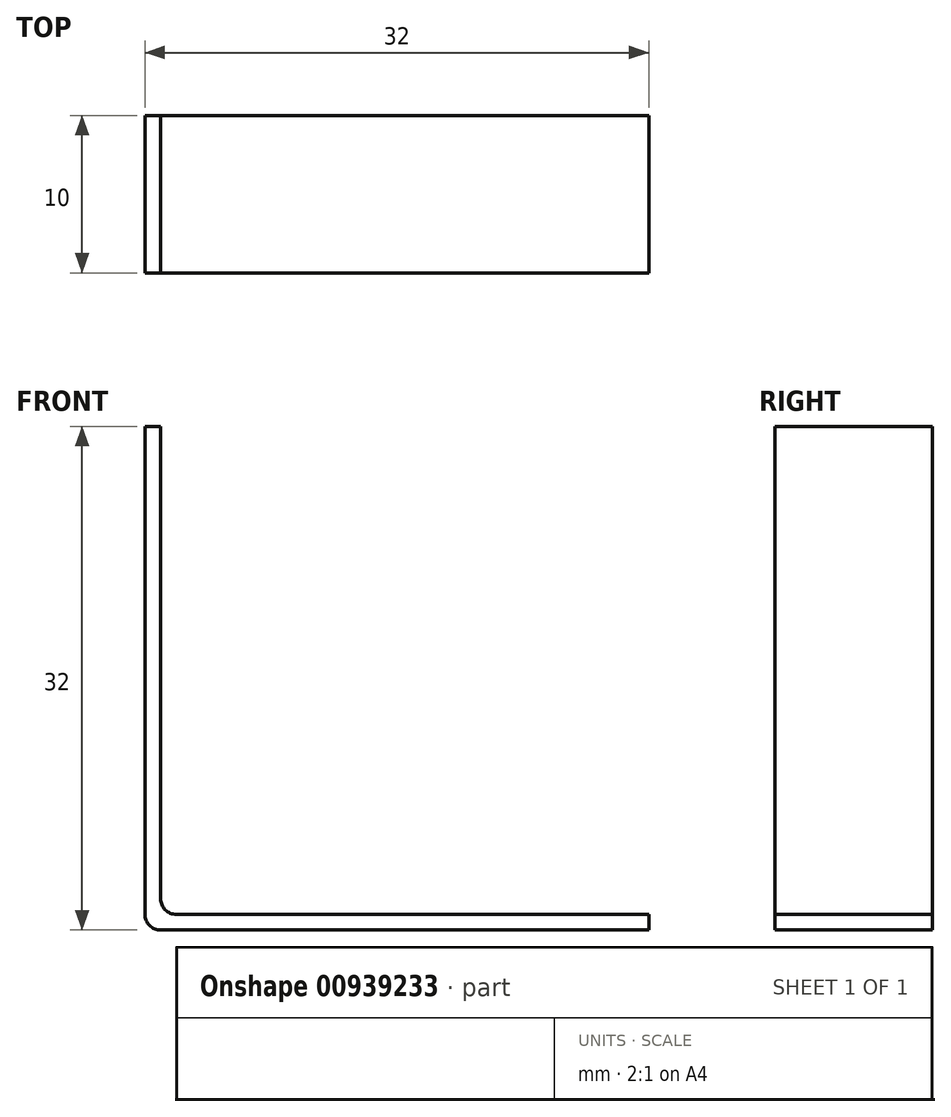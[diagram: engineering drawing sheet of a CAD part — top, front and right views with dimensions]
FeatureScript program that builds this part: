
annotation { "Feature Type Name" : "Feature", "Feature Type Description" : "" }
export const myFeature = defineFeature(function(context is Context, id is Id, definition is map)
    precondition{}
    {
        {
            var Q0;
            Q0=qCreatedBy(makeId("Front.planeOp"),FACE);
            var sketch = newSketch(context, id + "F0", { "sketchPlane" : qUnion([Q0])});
            skLineSegment(sketch, "E0", {"start": v(0, 1) * mm, "end": v(0, 31) * mm});
            skLineSegment(sketch, "E1", {"start": v(0, 31) * mm, "end": v(-1, 31) * mm});
            skLineSegment(sketch, "E2", {"start": v(-1, 31) * mm, "end": v(-1, 0) * mm});
            skLineSegment(sketch, "E3", {"start": v(0, -1) * mm, "end": v(31, -1) * mm});
            skLineSegment(sketch, "E4", {"start": v(31, -1) * mm, "end": v(31, 0) * mm});
            skLineSegment(sketch, "E5", {"start": v(31, 0) * mm, "end": v(1, 0) * mm});
            skPoint(sketch, "E6.visualSharp", {"position": v(0, 0) * mm});
            skArc(sketch, "E6.filletArc", {"start": v(0, 1) * mm, "mid": v(0.3, 0.3) * mm, "end": v(1, 0) * mm});
            skPoint(sketch, "E7.visualSharp", {"position": v(-1, -1) * mm});
            skArc(sketch, "E7.filletArc", {"start": v(-1, 0) * mm, "mid": v(-0.7, -0.7) * mm, "end": v(0, -1) * mm});
            skSolve(sketch);
        }
        {
            var Q0;
            Q0=makeQuery(id+"F0.imprint","IMPRINT",FACE,{"disambiguationData":[TD([[makeQuery(id+"F0.imprint","IMPRINT",EDGE,{"derivedFrom":sQuery(id+"F0.wireOp",EDGE,"E0")}),1.0]])]});
            extrude(context, id + "F1", {"entities" : qUnion([Q0]), "depth" : 10 * mm, "offsetDistance" : 25 * mm});
        }
    });
